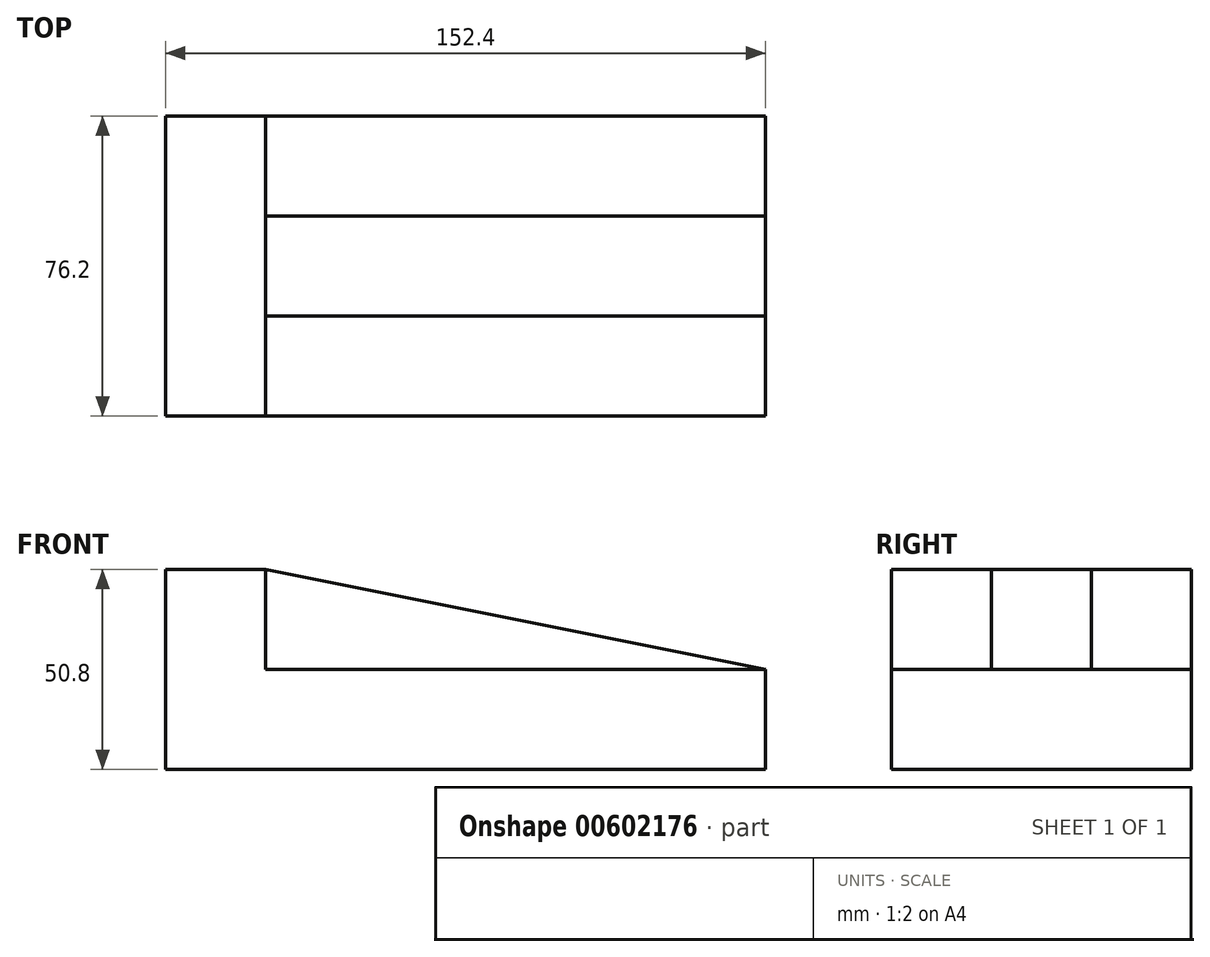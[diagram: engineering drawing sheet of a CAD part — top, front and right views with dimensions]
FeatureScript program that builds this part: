
annotation { "Feature Type Name" : "Feature", "Feature Type Description" : "" }
export const myFeature = defineFeature(function(context is Context, id is Id, definition is map)
    precondition{}
    {
        {
            var Q0;
            Q0=qCreatedBy(makeId("Front.planeOp"),FACE);
            var sketch = newSketch(context, id + "F0", { "sketchPlane" : qUnion([Q0])});
            skLineSegment(sketch, "E0", {"start": v(0, 0) * mm, "end": v(152.4, 0) * mm});
            skLineSegment(sketch, "E1", {"start": v(152.4, 0) * mm, "end": v(152.4, 25.4) * mm});
            skLineSegment(sketch, "E2", {"start": v(152.4, 25.4) * mm, "end": v(25.4, 25.4) * mm});
            skLineSegment(sketch, "E3", {"start": v(25.4, 25.4) * mm, "end": v(25.4, 50.8) * mm});
            skLineSegment(sketch, "E4", {"start": v(25.4, 50.8) * mm, "end": v(0, 50.8) * mm});
            skLineSegment(sketch, "E5", {"start": v(0, 50.8) * mm, "end": v(0, 0) * mm});
            skSolve(sketch);
        }
        {
            var Q0;
            Q0=makeQuery(id+"F0.imprint","IMPRINT",FACE,{"disambiguationData":[TD([[makeQuery(id+"F0.imprint","IMPRINT",EDGE,{"derivedFrom":sQuery(id+"F0.wireOp",EDGE,"E0")}),1.0]])]});
            extrude(context, id + "F1", {"entities" : qUnion([Q0]), "oppositeDirection" : true, "depth" : 76.2 * mm, "offsetDistance" : 25.4 * mm});
        }
        {
            var Q0;
            Q0=makeQuery(id+"F1.opExtrude","SWEPT_FACE",FACE,{"disambiguationData":[OSD([sQuery(id+"F0.wireOp",EDGE,"E2")])]});
            var sketch = newSketch(context, id + "F2", { "sketchPlane" : qUnion([Q0])});
            skLineSegment(sketch, "E6", {"start": v(25.4, 50.8) * mm, "end": v(152.4, 50.8) * mm});
            skLineSegment(sketch, "E7", {"start": v(152.4, 50.8) * mm, "end": v(152.4, 25.4) * mm});
            skLineSegment(sketch, "E8", {"start": v(152.4, 25.4) * mm, "end": v(25.4, 25.4) * mm});
            skLineSegment(sketch, "E9", {"start": v(25.4, 25.4) * mm, "end": v(25.4, 50.8) * mm});
            skSolve(sketch);
        }
        {
            var Q0;
            Q0=makeQuery(id+"F2.imprint","IMPRINT",FACE,{"disambiguationData":[TD([[makeQuery(id+"F2.imprint","IMPRINT",EDGE,{"derivedFrom":sQuery(id+"F2.wireOp",EDGE,"E6")}),-1.0]])]});
            extrude(context, id + "F3", {"entities" : qUnion([Q0]), "operationType" : NewBodyOperationType.ADD, "depth" : 25.4 * mm, "offsetDistance" : 25.4 * mm});
        }
        {
            var Q0;
            Q0=makeQuery(id+"F3.opExtrude","SWEPT_FACE",FACE,{"disambiguationData":[OSD([sQuery(id+"F2.wireOp",EDGE,"E8")])]});
            var sketch = newSketch(context, id + "F4", { "sketchPlane" : qUnion([Q0])});
            skLineSegment(sketch, "E10", {"start": v(152.4, 25.4) * mm, "end": v(25.4, 50.8) * mm});
            skSolve(sketch);
        }
        {
            var Q0;
            Q0=makeQuery(id+"F4.imprint","IMPRINT",FACE,{"disambiguationData":[TD([[makeQuery(id+"F4.imprint","IMPRINT",EDGE,{"derivedFrom":sQuery(id+"F4.wireOp",EDGE,"E10")}),-1.0]])]});
            extrude(context, id + "F5", {"entities" : qUnion([Q0]), "operationType" : NewBodyOperationType.REMOVE, "oppositeDirection" : true, "depth" : 25.4 * mm, "offsetDistance" : 25.4 * mm});
        }
    });
